# Revit family: Hager-UNIVERS-Surface_mounted-IP44-With_Cover-With_DIN-Hosted-GB-en
name_source: partatom
category: Electrical Equipment
units: mm (PartAtom-declared; Revit-internal decimal feet)

## family parameters
Cut with Voids When Loaded = No
Host = Face
Maintain Annotation Orientation = Yes
Panel Configuration = Two Columns, Circuits Across
Part Type = Panelboard
Room Calculation Point = No
Round Connector Dimension = Use Diameter
Shared = No

## types (8) — shared parameters
BC_MODEL_ID = 1554471
BC_OBJECT_ID = 513933
BC_OBJECT_VERSION = #1
Code hager = ADD-EC000214_EU
EF000007 - Colour = White
EF000024 - UV resistant = No
EF000049 - Depth = 165 mm  [stored 0.541339 ft]
EF000116 - RAL number = 9010
EF000118 - With mounting plate = No
EF000218 - Recess depth = 161 mm  [stored 0.528215 ft]
EF001062 - EMC-version = No
EF001088 - Extension possible = Yes
EF001134 - With DIN-rail = Yes
EF004462 - Type of closure = Other
EF005474 - Degree of protection (IP rating) = IP44
EF006244 - Transparent cover/door = No
EF006306 - With lock = No
EF009212 - Cover model = With notch
EF015777 - Neutral terminal block = Yes
EF015941 - Signal passing door = No
ETIM class code = EC000214
ETIM class name = Small distribution board
HG000002-With door or cover = Yes
HG000003-Range = UNIVERS
HG000005-Thickness = 2 mm  [stored 0.00656168 ft]
HG000006-Flush mounted = No
HG000011-Empty rows from bottom = No
HG000012-Door swing angle = 90.00°
HG000013-Door on the left = No
HG000014-Door on the right = Yes
HG000015-Clearance visibility = Yes
HG000016-Door 3D visibility = Yes
HG000017-Distance between poles = 18 mm  [stored 0.0590551 ft]
HG000060-RAL-number = 9010
HG000099-Onfly Template ID = 507532
Manufacturer = Hager
Name = UNIVERS-Surface_mounted-IP44-With_Cover-With_DIN-GB
Name BIM&CO = Electricity
Name hager = ADD_Enclosures_EC000214
Uniformat = Low Tension Service & Dist.
Uniformat code = D501001
zero-valued in all types: Default Elevation, EF001131 - Internal depth, HG000007-Number of empty columns, HG000008-Number of empty rows

## per-type parameters (varying)
| type | BC_VARIANT_ID | EF000003 - Mounting method | EF000008 - Width | EF000040 - Height | EF000266 - Number of rows | EF000332 - Recess height | EF000846 - Recess width | EF002950 - Width in number of modular spacings | EF015776 - Earthing terminal block | HG000001-Number of columns | HG000004-Manufacturer reference | HG000009-Double swing door | HG000010-Asymmetric doors | HGEF000266-Number of rows | HGEF002950-Width in number of modular spacings |
| UNIVERS-Surface_mounted_W550_H650_D165_24_Modular_Spacing-FWB42 | 1179176 | Surface mounted | 550 mm | 650 mm  [stored 2.13255 ft] | 4 | 650 mm  [stored 2.13255 ft] | 550 mm | 24 | No | 2 | FWB42 | No | No | 4 | 24 |
| UNIVERS-Surface_mounted_W550_H650_D165_24_Modular_Spacing-FWB42S | 1179177 | Surface mounted/recessed mounted | 550 mm | 650 mm  [stored 2.13255 ft] | 4 | 650 mm  [stored 2.13255 ft] | 550 mm | 24 | Yes | 2 | FWB42S | No | No | 4 | 24 |
| UNIVERS-Surface_mounted_W550_H1100_D165_24_Modular_Spacing-FWB72 | 1179178 | Surface mounted | 550 mm | 1100 mm | 7 | 1100 mm | 550 mm | 24 | No | 2 | FWB72 | No | No | 7 | 24 |
| UNIVERS-Surface_mounted_W550_H1100_D165_24_Modular_Spacing-FWB72S | 1179180 | Surface mounted/recessed mounted | 550 mm | 1100 mm | 7 | 1100 mm | 550 mm | 24 | Yes | 2 | FWB72S | No | No | 7 | 24 |
| UNIVERS-Surface_mounted_W800_H1100_D165_36_Modular_Spacing-FWB73 | 1179181 | Surface mounted | 800 mm  [stored 2.62467 ft] | 1100 mm | 7 | 1100 mm | 800 mm  [stored 2.62467 ft] | 36 | No | 3 | FWB73 | Yes | Yes | 7 | 36 |
| UNIVERS-Surface_mounted_W800_H1100_D165_36_Modular_Spacing-FWB73S | 1179182 | Surface mounted/recessed mounted | 800 mm  [stored 2.62467 ft] | 1100 mm | 7 | 1100 mm | 800 mm  [stored 2.62467 ft] | 36 | Yes | 3 | FWB73S | Yes | Yes | 7 | 36 |
| UNIVERS-Surface_mounted_W1050_H1100_D165_48_Modular_Spacing-FWB74 | 1179183 | Surface mounted | 1050 mm | 1100 mm | 7 | 1100 mm | 1050 mm | 48 | No | 4 | FWB74 | Yes | No | 7 | 48 |
| UNIVERS-Surface_mounted_W1050_H1100_D165_48_Modular_Spacing-FWB74S | 1179184 | Surface mounted/recessed mounted | 1050 mm | 1100 mm | 7 | 1100 mm | 1050 mm | 48 | Yes | 4 | FWB74S | Yes | No | 7 | 48 |

note: column(s) folded — value = type name in every type: Reference

note: [stored X ft] marks values corroborated as IEEE doubles in the binary element streams (Revit-internal decimal feet)

## geometry (parser evidence)
native form markers: Sweep x16
no freeform markers — native parametric forms only
